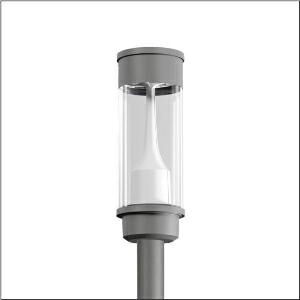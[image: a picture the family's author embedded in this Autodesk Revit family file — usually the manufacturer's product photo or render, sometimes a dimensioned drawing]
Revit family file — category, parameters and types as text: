
# Revit family: litepole_iq___st1_2a_5xa5415mf14h_d5a4
name_source: partatom
category: Lighting Fixtures
units: mm (PartAtom-declared; Revit-internal decimal feet)

## family parameters
Cut with Voids When Loaded = No
Host = Face
Light Source = No
Part Type = Normal
Room Calculation Point = No
Round Connector Dimension = Use Diameter
Shared = No

## types (1)
- --- (1 x LED, 1540 lm, 11.8 W, 2700K)
    Apparent Load = 12 VA
    CIE Flux Codes = 22 61 93 96 100
    Color Rendering = 70
    Color Temperature = 2700K
    Default Elevation = 1800 mm
    Description = Litepole iQ, mast luminaire, Module 540 iQ-SR, primary light control with 3 zone facetted reflector, of plastic, silver coated, highly specular, structured, primary optical cover: cover, of PMMA, transparent, partly coated, light distribution: ST1.2a, light emission: direct distribution, primary light characteristic: asymmetric, installation type: post-top, LED, High Power LED, rated luminous flux: 1.540lm, luminous efficacy: 131lm/W, light colour: 727, colour temperature: 2700K, control gear: ECG iQ, control: optimised constant luminous flux control (CLO 2.0), Desk-Remote (wireless, voltage-free reading and setting of iQ features in the workshop via application-optimized NFC function/RFID function), Light-Fading, Smart-Wire, Night-Set, Lumen-Switch, Temp-Guard, Auto-Match, Street-Remote, presetting dimming logarithmic, with terminal, 6-pole, max. 2.5mm², mains connection: 230..240V, AC, 50/60Hz, start of lifetime: 12W, end of service life: 12W, reduction: 6W, luminaire housing, upper part, of glass-fibre reinforced polyester, coated, Siteco® metallic grey (DB 702S), diameter: 210mm, height: 590mm, spigot size: d x l = 76 x 70mm (post-top) | with reducer (optional accessory) 60 x 70mm, post-top mast mounting element, of diecast aluminium, coated, Siteco® metallic grey (DB 702S), Module 540 iQ-SR, traffic white (RAL 9016), equipment: standard, protection rating (complete): IP65, insulation class (complete): insulation class II (safety insulation), certification: CE, ENEC, VDE, packaging unit: 1 piece

Light Distribution: ST1.2a
    Height = 590 mm
    Lamp = 1 x LED
    Lamp Light Flux = 1540 lm
    Lamp Power = 11.8 W
    Lamp count = 1
    Length = 220 mm
    Luminous efficacy = 131 lm/W
    Manufacturer = Siteco
    ModVariant = No
    Model = 5XA5415MF14H
    Number of Poles = 1
    OnlyDefault = Yes
    Power Factor = 1
    Product Name = Litepole iQ | ST1.2a
    Product group = mast luminaire | pylon top
    ProductGroupID = 6100
    Protection Class = Protection class II
    Protection Degree = IP 65
    RLX_Detail_Level = 1
    RLX_Emergency_Light_Flux = 0 lm
    RLX_Emergency_Type = 0
    RLX_Emergency_Type_DB = No
    RlxData = <blob elided: 71861 chars, md5=7dc5a305>
    Socket = socket
    Standby Power = 0 W
    System Light Flux = 1540 lm
    System Power = 12 W
    Type Comments = factory setting: luminous flux: 100 % | dim-lin: 254 | 472 mA
    Type Image = l_1006025.jpg
    URL = http://relux.com
    VarID = @adj_085327
    Voltage = 0 V
    Weight = 0.00 kg
    Width = 0 mm  [stored 0 ft]

note: [stored X ft] marks values corroborated as IEEE doubles in the binary element streams (Revit-internal decimal feet)

## geometry (parser evidence)
native form markers: Blend x4, Sweep x11
no freeform markers — native parametric forms only
